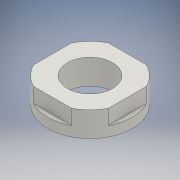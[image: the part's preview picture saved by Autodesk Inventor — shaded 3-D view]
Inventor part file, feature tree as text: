
AUTODESK INVENTOR PART (.ipt)
format: ipt  version: 2017 (Build 210142000, 142)  size: 114,176 bytes
history: native  units: mm
features: extrude x2, sketch x2
ambient origin geometry x8: Origin, YZ Plane, XZ Plane, XY Plane, X Axis, Y Axis, Z Axis, Center Point
bodies: Solid1 (feature_tree)
feature tree (4):
  extrude  "Extrusion1"  Depth=16.8mm
  extrude  "Extrusion2"  Depth=15.0mm
  sketch  "Sketch1"  dims[d0=9.02mm d1=16.8mm]
  sketch  "Sketch2"  dims[d2=5.0mm d3=0.0mm d4=15.0mm d5=3.0mm d6=0.0mm]
